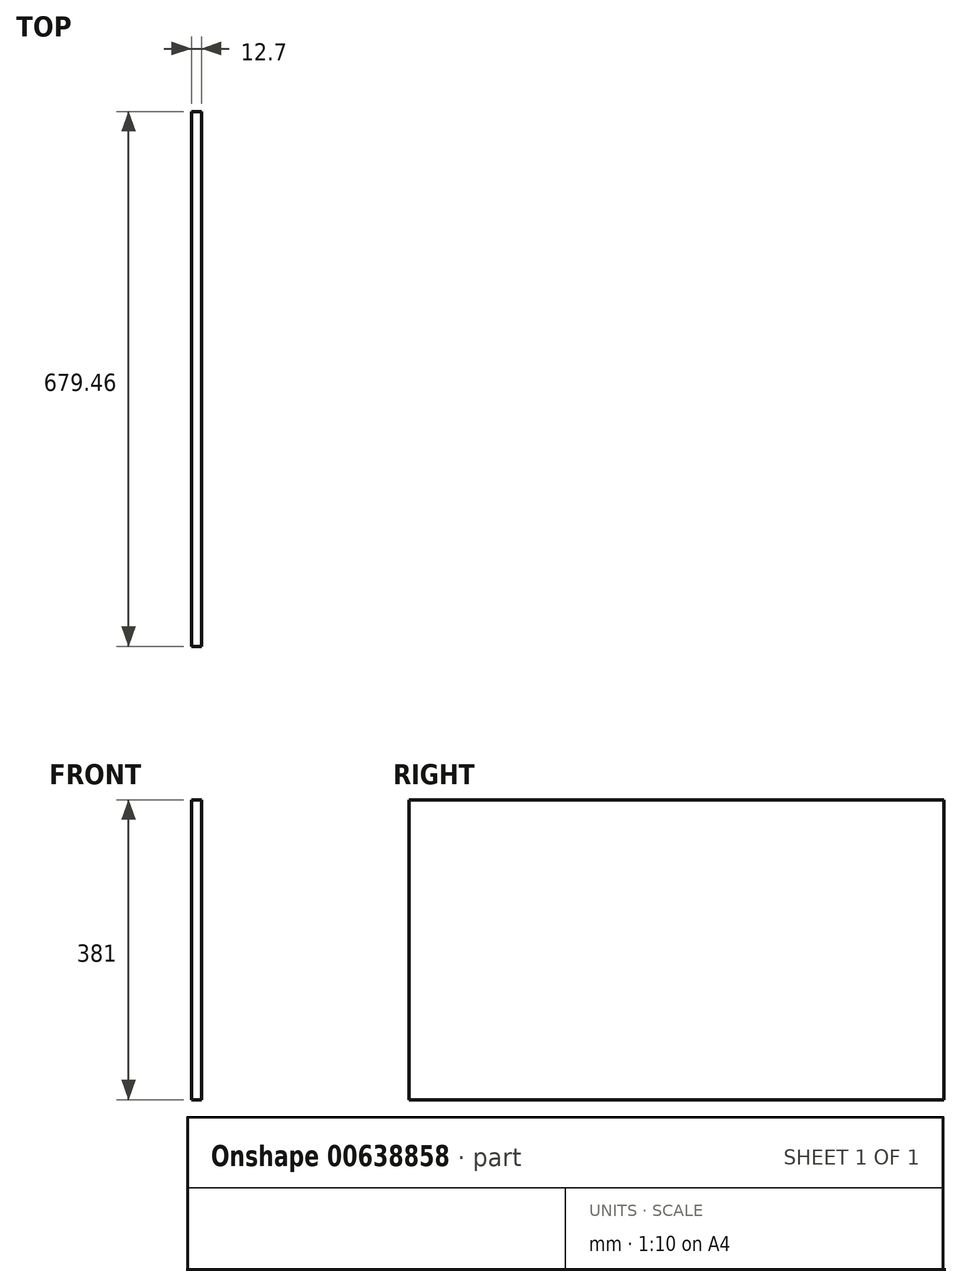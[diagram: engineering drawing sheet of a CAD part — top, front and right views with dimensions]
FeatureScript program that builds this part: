
annotation { "Feature Type Name" : "Feature", "Feature Type Description" : "" }
export const myFeature = defineFeature(function(context is Context, id is Id, definition is map)
    precondition{}
    {
        {
            var Q0;
            Q0=qCreatedBy(makeId("Right.planeOp"),FACE);
            var sketch = newSketch(context, id + "F0", { "sketchPlane" : qUnion([Q0])});
            skLineSegment(sketch, "E0.bottom", {"start": v(339.73, 190.5) * mm, "end": v(-339.73, 190.5) * mm});
            skLineSegment(sketch, "E0.top", {"start": v(339.73, -190.5) * mm, "end": v(-339.73, -190.5) * mm});
            skLineSegment(sketch, "E0.left", {"start": v(339.73, 190.5) * mm, "end": v(339.73, -190.5) * mm});
            skLineSegment(sketch, "E0.right", {"start": v(-339.73, 190.5) * mm, "end": v(-339.73, -190.5) * mm});
            skPoint(sketch, "E0.middle", {"position": v(0, 0) * mm});
            skSolve(sketch);
        }
        {
            var Q0;
            Q0=makeQuery(id+"F0.imprint","IMPRINT",FACE,{"disambiguationData":[TD([[makeQuery(id+"F0.imprint","IMPRINT",EDGE,{"derivedFrom":sQuery(id+"F0.wireOp",EDGE,"E0.bottom")}),1.0]])]});
            extrude(context, id + "F1", {"entities" : qUnion([Q0]), "depth" : 12.7 * mm, "offsetDistance" : 25.4 * mm});
        }
    });
